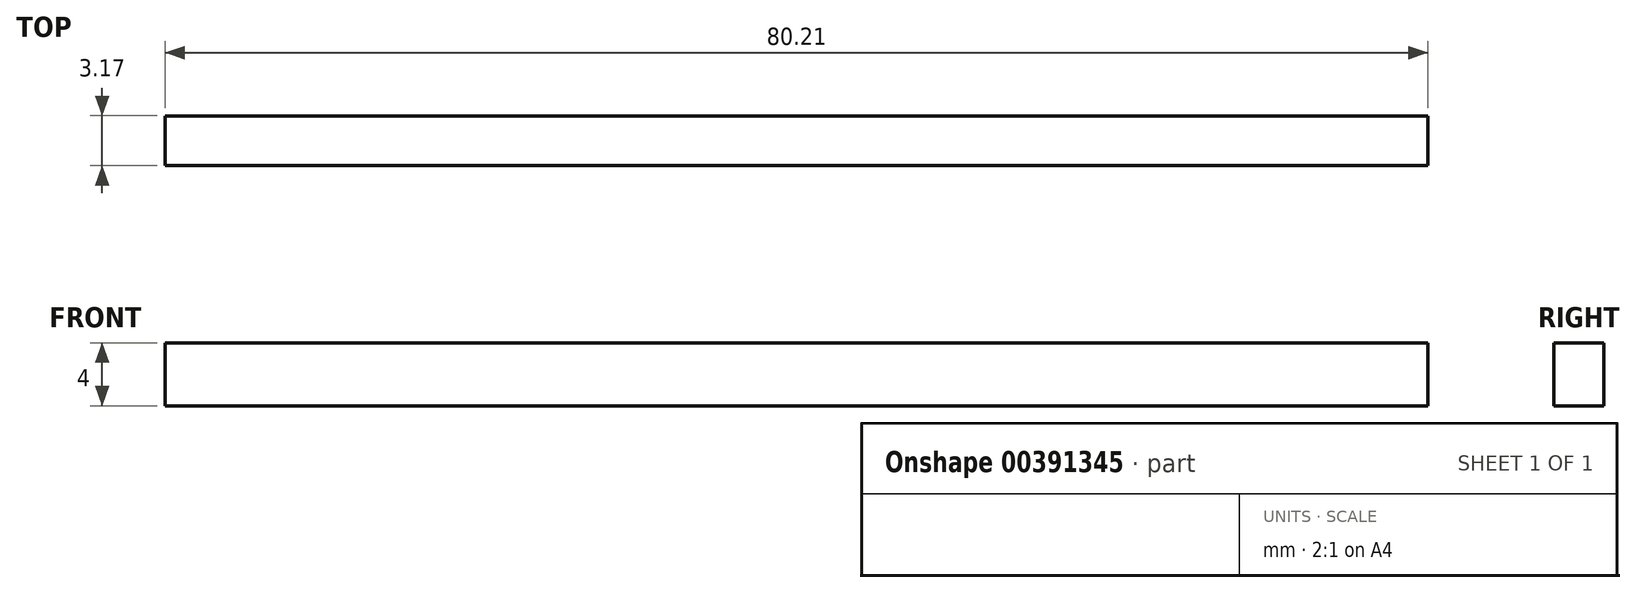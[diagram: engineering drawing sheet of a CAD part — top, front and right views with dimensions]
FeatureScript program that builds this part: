
annotation { "Feature Type Name" : "Feature", "Feature Type Description" : "" }
export const myFeature = defineFeature(function(context is Context, id is Id, definition is map)
    precondition{}
    {
        {
            var Q0;
            Q0=qCreatedBy(makeId("Top.planeOp"),FACE);
            var sketch = newSketch(context, id + "F0", { "sketchPlane" : qUnion([Q0])});
            skText(sketch, "E0", { "text": "Equipos", "fontName": "OpenSans-Italic.ttf"});
            const initialGuessF0  = {"E0": [-0.08, 0.02481, 1, 0, 0.01631]};
            skSetInitialGuess(sketch, initialGuessF0);
            skSolve(sketch);
        }
        {
            var Q0;
            Q0=qCreatedBy(makeId("Top.planeOp"),FACE);
            var sketch = newSketch(context, id + "F1", { "sketchPlane" : qUnion([Q0])});
            skLineSegment(sketch, "E1.bottom", {"start": v(-80.2, 27.93) * mm, "end": v(0, 27.93) * mm});
            skLineSegment(sketch, "E1.top", {"start": v(-80.2, 24.76) * mm, "end": v(0, 24.76) * mm});
            skLineSegment(sketch, "E1.left", {"start": v(-80.2, 27.93) * mm, "end": v(-80.2, 24.76) * mm});
            skLineSegment(sketch, "E1.right", {"start": v(0, 27.93) * mm, "end": v(0, 24.76) * mm});
            skSolve(sketch);
        }
        {
            var Q0;
            Q0=makeQuery(id+"F1.imprint","IMPRINT",FACE,{"disambiguationData":[TD([[makeQuery(id+"F1.imprint","IMPRINT",EDGE,{"derivedFrom":sQuery(id+"F1.wireOp",EDGE,"E1.bottom")}),-1.0]])]});
            extrude(context, id + "F2", {"entities" : qUnion([Q0]), "depth" : 4 * mm});
        }
    });
